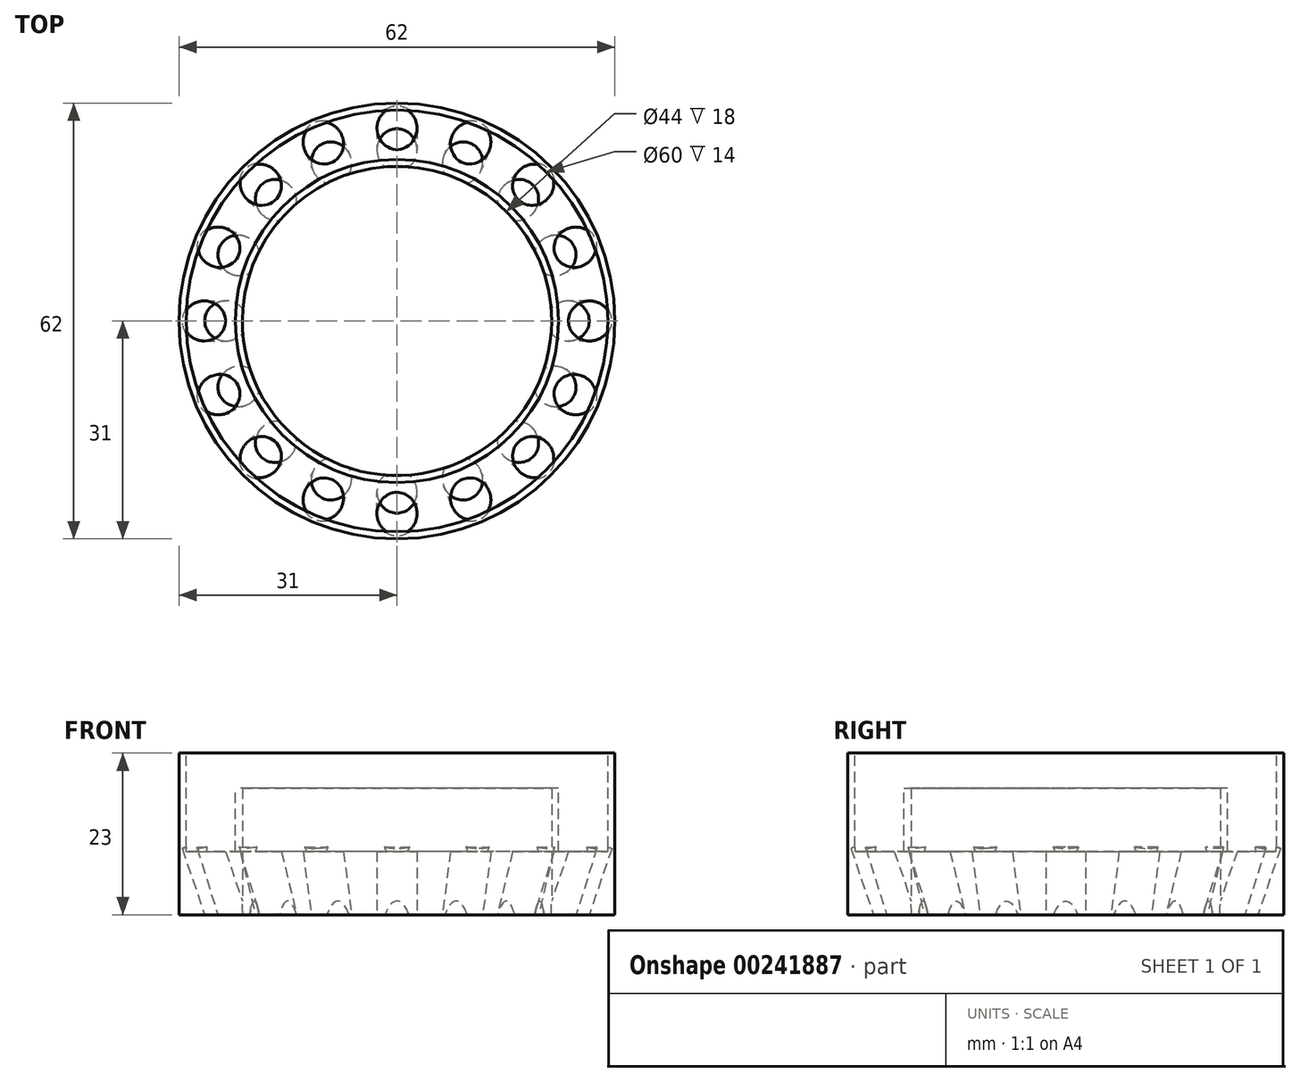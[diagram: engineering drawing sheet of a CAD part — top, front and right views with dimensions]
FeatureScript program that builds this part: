
annotation { "Feature Type Name" : "Feature", "Feature Type Description" : "" }
export const myFeature = defineFeature(function(context is Context, id is Id, definition is map)
    precondition{}
    {
        {
            var Q0;
            Q0=qCreatedBy(makeId("Top.planeOp"),FACE);
            var sketch = newSketch(context, id + "F0", { "sketchPlane" : qUnion([Q0])});
            skCircle(sketch, "E0", {"center": v(0, 0) * mm, "radius": 31 * mm});
            skCircle(sketch, "E1", {"center": v(0, 0) * mm, "radius": 22 * mm});
            skSolve(sketch);
        }
        {
            var Q0;
            Q0 = qSketchRegion(id + "F0", true);
            extrude(context, id + "F1", {"entities" : qUnion([Q0]), "depth" : 23 * mm});
        }
        {
            var Q0;
            Q0=makeQuery(id+"F1.opExtrude","CAP_FACE",FACE,{"disambiguationData":[OSD([sQuery(id+"F0.wireOp",EDGE,"E0"),sQuery(id+"F0.wireOp",EDGE,"E1")])],"isStart":false});
            var sketch = newSketch(context, id + "F2", { "sketchPlane" : qUnion([Q0])});
            skCircle(sketch, "E2", {"center": v(0, 0) * mm, "radius": 30 * mm});
            skCircle(sketch, "E3", {"center": v(0, 0) * mm, "radius": 23 * mm});
            skSolve(sketch);
        }
        {
            var Q0;
            Q0 = qSketchRegion(id + "F2", true);
            extrude(context, id + "F3", {"entities" : qUnion([Q0]), "operationType" : NewBodyOperationType.REMOVE, "oppositeDirection" : true, "depth" : 14 * mm});
        }
        {
            var Q0;
            {var subQ0=sQuery(id+"F0.wireOp",EDGE,"E1");Q0=makeQuery(id+"F3.boolean.opBoolean","SPLIT",FACE,{"disambiguationData":[TD([makeQuery(id+"F1.opExtrude","SWEPT_FACE",FACE,{"disambiguationData":[OSD([subQ0])]})])],"derivedFrom":makeQuery(id+"F1.opExtrude","CAP_FACE",FACE,{"disambiguationData":[OSD([sQuery(id+"F0.wireOp",EDGE,"E0"),subQ0])],"isStart":false})});}
            var sketch = newSketch(context, id + "F4", { "sketchPlane" : qUnion([Q0])});
            skCircle(sketch, "E4", {"center": v(0, 0) * mm, "radius": 24.74 * mm});
            skSolve(sketch);
        }
        {
            var Q0;
            Q0 = qSketchRegion(id + "F4", true);
            extrude(context, id + "F5", {"entities" : qUnion([Q0]), "operationType" : NewBodyOperationType.REMOVE, "oppositeDirection" : true, "depth" : 5 * mm});
        }
        {
            var Q0;
            Q0=qCreatedBy(makeId("Right.planeOp"),FACE);
            var sketch = newSketch(context, id + "F6", { "sketchPlane" : qUnion([Q0])});
            skLineSegment(sketch, "E5", {"start": v(0, -71.5) * mm, "end": v(34.22, 29.02) * mm, "construction": true});
            skLineSegment(sketch, "E6", {"start": v(26.7, -1.92) * mm, "end": v(24, -1) * mm});
            skSolve(sketch);
        }
        {
            var Q0;
            Q0=qCreatedBy(makeId("Right.planeOp"),FACE);
            var sketch = newSketch(context, id + "F7", { "sketchPlane" : qUnion([Q0])});
            skLineSegment(sketch, "E7", {"start": v(0, -61.77) * mm, "end": v(0, 47.03) * mm});
            skSolve(sketch);
        }
        {
            var Q0;
            Q0 = qSketchRegion(id + "F6", true);
            var Q1;
            Q1=sQuery(id+"F6.wireOp",EDGE,"E6");
            var Q2;
            Q2=sQuery(id+"F6.wireOp",EDGE,"E5");
            revolve(context, id + "F8", {"bodyType" : ToolBodyType.SURFACE, "entities" : qUnion([Q0]), "surfaceEntities" : qUnion([Q1]), "axis" : qUnion([Q2]), "revolveType" : RevolveType.FULL});
        }
        {
            var Q0;
            Q0=makeQuery(id+"F8.opRevolve","SWEPT_BODY",BODY,{"disambiguationData":[OSD([sQuery(id+"F6.wireOp",EDGE,"E6")])]});
            var Q1;
            Q1=sQuery(id+"F7.wireOp",EDGE,"E7");
            circularPattern(context, id + "F9", {"entities" : qUnion([Q0]), "axis" : qUnion([Q1]), "angle" : 360 * degree, "instanceCount" : 16, "equalSpace" : true});
        }
        {
            var Q0;
            Q0=makeQuery(id+"F9.opPattern","COPY",FACE,{"derivedFrom":makeQuery(id+"F8.opRevolve","SWEPT_FACE",FACE,{"disambiguationData":[OSD([sQuery(id+"F6.wireOp",EDGE,"E6")])]}),"instanceName":"15"});
            extrude(context, id + "F10", {"entities" : qUnion([Q0]), "operationType" : NewBodyOperationType.REMOVE, "oppositeDirection" : true, "depth" : 12 * mm});
        }
        {
            var Q0;
            Q0=makeQuery(id+"F8.opRevolve","SWEPT_FACE",FACE,{"disambiguationData":[OSD([sQuery(id+"F6.wireOp",EDGE,"E6")])]});
            extrude(context, id + "F11", {"entities" : qUnion([Q0]), "operationType" : NewBodyOperationType.REMOVE, "oppositeDirection" : true, "depth" : 12 * mm});
        }
        {
            var Q0;
            Q0=makeQuery(id+"F9.opPattern","COPY",FACE,{"derivedFrom":makeQuery(id+"F8.opRevolve","SWEPT_FACE",FACE,{"disambiguationData":[OSD([sQuery(id+"F6.wireOp",EDGE,"E6")])]}),"instanceName":"1"});
            extrude(context, id + "F12", {"entities" : qUnion([Q0]), "operationType" : NewBodyOperationType.REMOVE, "oppositeDirection" : true, "depth" : 12 * mm});
        }
        {
            var Q0;
            Q0=makeQuery(id+"F9.opPattern","COPY",FACE,{"derivedFrom":makeQuery(id+"F8.opRevolve","SWEPT_FACE",FACE,{"disambiguationData":[OSD([sQuery(id+"F6.wireOp",EDGE,"E6")])]}),"instanceName":"2"});
            extrude(context, id + "F13", {"entities" : qUnion([Q0]), "operationType" : NewBodyOperationType.REMOVE, "oppositeDirection" : true, "depth" : 12 * mm});
        }
        {
            var Q0;
            Q0=makeQuery(id+"F9.opPattern","COPY",FACE,{"derivedFrom":makeQuery(id+"F8.opRevolve","SWEPT_FACE",FACE,{"disambiguationData":[OSD([sQuery(id+"F6.wireOp",EDGE,"E6")])]}),"instanceName":"3"});
            extrude(context, id + "F14", {"entities" : qUnion([Q0]), "operationType" : NewBodyOperationType.REMOVE, "oppositeDirection" : true, "depth" : 12 * mm});
        }
        {
            var Q0;
            Q0=makeQuery(id+"F9.opPattern","COPY",FACE,{"derivedFrom":makeQuery(id+"F8.opRevolve","SWEPT_FACE",FACE,{"disambiguationData":[OSD([sQuery(id+"F6.wireOp",EDGE,"E6")])]}),"instanceName":"4"});
            extrude(context, id + "F15", {"entities" : qUnion([Q0]), "operationType" : NewBodyOperationType.REMOVE, "oppositeDirection" : true, "depth" : 12 * mm});
        }
        {
            var Q0;
            Q0=makeQuery(id+"F9.opPattern","COPY",FACE,{"derivedFrom":makeQuery(id+"F8.opRevolve","SWEPT_FACE",FACE,{"disambiguationData":[OSD([sQuery(id+"F6.wireOp",EDGE,"E6")])]}),"instanceName":"5"});
            extrude(context, id + "F16", {"entities" : qUnion([Q0]), "operationType" : NewBodyOperationType.REMOVE, "oppositeDirection" : true, "depth" : 12 * mm});
        }
        {
            var Q0;
            Q0=makeQuery(id+"F9.opPattern","COPY",FACE,{"derivedFrom":makeQuery(id+"F8.opRevolve","SWEPT_FACE",FACE,{"disambiguationData":[OSD([sQuery(id+"F6.wireOp",EDGE,"E6")])]}),"instanceName":"6"});
            extrude(context, id + "F17", {"entities" : qUnion([Q0]), "operationType" : NewBodyOperationType.REMOVE, "oppositeDirection" : true, "depth" : 12 * mm});
        }
        {
            var Q0;
            Q0=makeQuery(id+"F9.opPattern","COPY",FACE,{"derivedFrom":makeQuery(id+"F8.opRevolve","SWEPT_FACE",FACE,{"disambiguationData":[OSD([sQuery(id+"F6.wireOp",EDGE,"E6")])]}),"instanceName":"7"});
            extrude(context, id + "F18", {"entities" : qUnion([Q0]), "operationType" : NewBodyOperationType.REMOVE, "oppositeDirection" : true, "depth" : 12 * mm});
        }
        {
            var Q0;
            Q0=makeQuery(id+"F9.opPattern","COPY",FACE,{"derivedFrom":makeQuery(id+"F8.opRevolve","SWEPT_FACE",FACE,{"disambiguationData":[OSD([sQuery(id+"F6.wireOp",EDGE,"E6")])]}),"instanceName":"8"});
            extrude(context, id + "F19", {"entities" : qUnion([Q0]), "operationType" : NewBodyOperationType.REMOVE, "oppositeDirection" : true, "depth" : 12 * mm});
        }
        {
            var Q0;
            Q0=makeQuery(id+"F9.opPattern","COPY",FACE,{"derivedFrom":makeQuery(id+"F8.opRevolve","SWEPT_FACE",FACE,{"disambiguationData":[OSD([sQuery(id+"F6.wireOp",EDGE,"E6")])]}),"instanceName":"9"});
            extrude(context, id + "F20", {"entities" : qUnion([Q0]), "operationType" : NewBodyOperationType.REMOVE, "oppositeDirection" : true, "depth" : 12 * mm});
        }
        {
            var Q0;
            Q0=makeQuery(id+"F9.opPattern","COPY",FACE,{"derivedFrom":makeQuery(id+"F8.opRevolve","SWEPT_FACE",FACE,{"disambiguationData":[OSD([sQuery(id+"F6.wireOp",EDGE,"E6")])]}),"instanceName":"10"});
            extrude(context, id + "F21", {"entities" : qUnion([Q0]), "operationType" : NewBodyOperationType.REMOVE, "oppositeDirection" : true, "depth" : 12 * mm});
        }
        {
            var Q0;
            Q0=makeQuery(id+"F9.opPattern","COPY",FACE,{"derivedFrom":makeQuery(id+"F8.opRevolve","SWEPT_FACE",FACE,{"disambiguationData":[OSD([sQuery(id+"F6.wireOp",EDGE,"E6")])]}),"instanceName":"11"});
            extrude(context, id + "F22", {"entities" : qUnion([Q0]), "operationType" : NewBodyOperationType.REMOVE, "oppositeDirection" : true, "depth" : 12 * mm});
        }
        {
            var Q0;
            Q0=makeQuery(id+"F9.opPattern","COPY",FACE,{"derivedFrom":makeQuery(id+"F8.opRevolve","SWEPT_FACE",FACE,{"disambiguationData":[OSD([sQuery(id+"F6.wireOp",EDGE,"E6")])]}),"instanceName":"12"});
            extrude(context, id + "F23", {"entities" : qUnion([Q0]), "operationType" : NewBodyOperationType.REMOVE, "oppositeDirection" : true, "depth" : 12 * mm});
        }
        {
            var Q0;
            Q0=makeQuery(id+"F9.opPattern","COPY",FACE,{"derivedFrom":makeQuery(id+"F8.opRevolve","SWEPT_FACE",FACE,{"disambiguationData":[OSD([sQuery(id+"F6.wireOp",EDGE,"E6")])]}),"instanceName":"13"});
            extrude(context, id + "F24", {"entities" : qUnion([Q0]), "operationType" : NewBodyOperationType.REMOVE, "oppositeDirection" : true, "depth" : 12 * mm});
        }
        {
            var Q0;
            Q0=makeQuery(id+"F9.opPattern","COPY",FACE,{"derivedFrom":makeQuery(id+"F8.opRevolve","SWEPT_FACE",FACE,{"disambiguationData":[OSD([sQuery(id+"F6.wireOp",EDGE,"E6")])]}),"instanceName":"14"});
            extrude(context, id + "F25", {"entities" : qUnion([Q0]), "operationType" : NewBodyOperationType.REMOVE, "oppositeDirection" : true, "depth" : 12 * mm});
        }
    });
